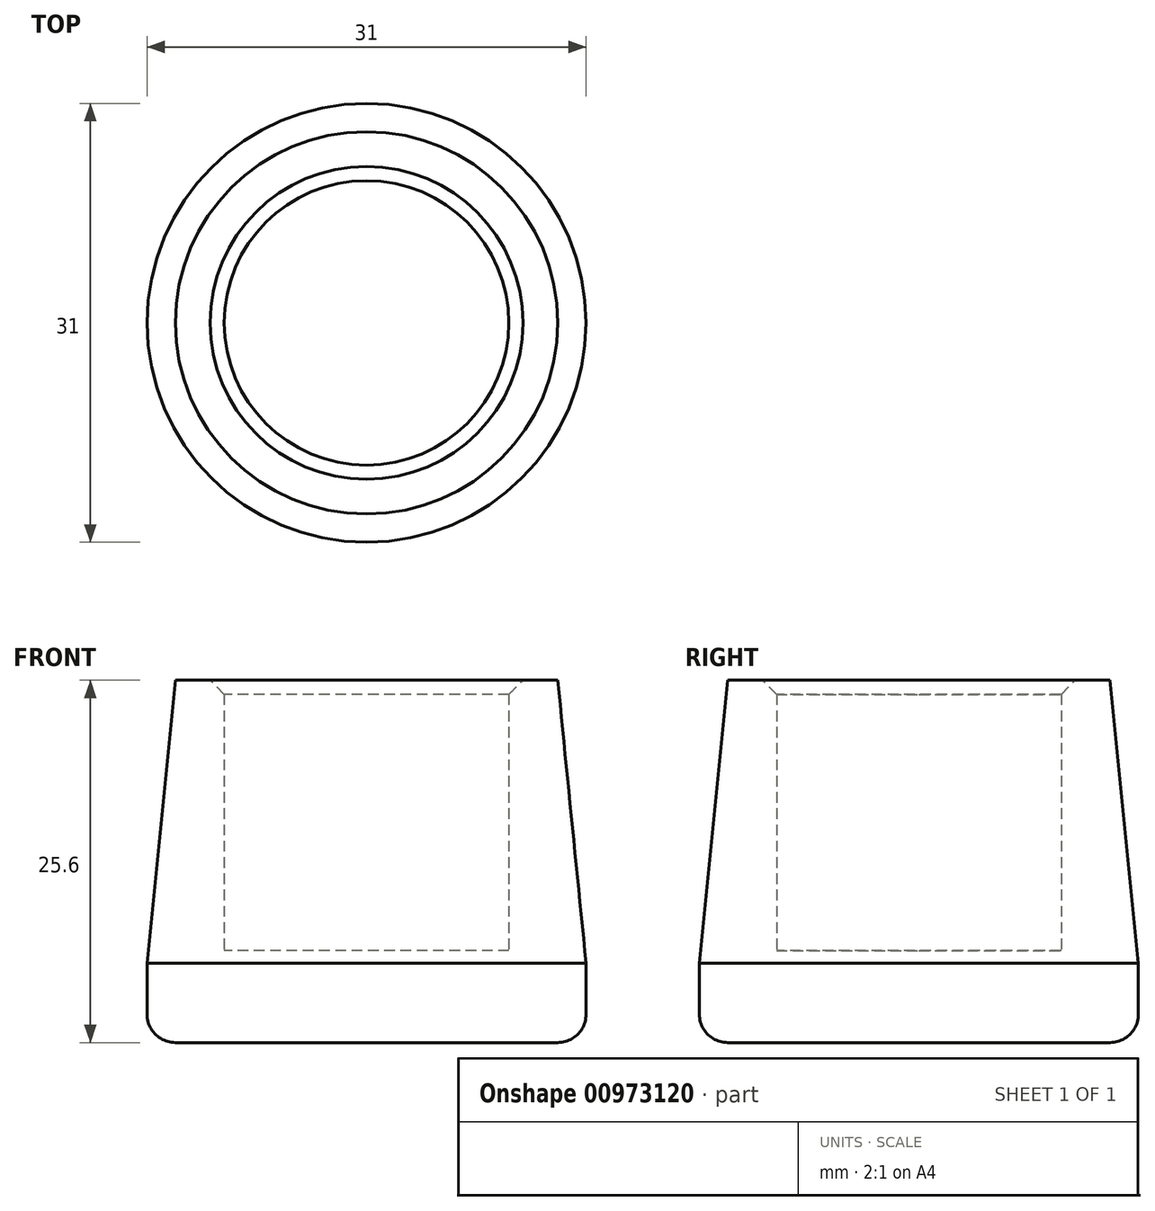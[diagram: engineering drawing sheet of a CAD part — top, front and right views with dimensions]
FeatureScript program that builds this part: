
annotation { "Feature Type Name" : "Feature", "Feature Type Description" : "" }
export const myFeature = defineFeature(function(context is Context, id is Id, definition is map)
    precondition{}
    {
        {
            var Q0;
            Q0=qCreatedBy(makeId("Top.planeOp"),FACE);
            var sketch = newSketch(context, id + "F0", { "sketchPlane" : qUnion([Q0])});
            skCircle(sketch, "E0", {"center": v(0, 0) * mm, "radius": 10.05 * mm});
            skCircle(sketch, "E1", {"center": v(0, 0) * mm, "radius": 15.5 * mm});
            skSolve(sketch);
        }
        {
            var Q0;
            Q0=makeQuery(id+"F0.imprint","IMPRINT",FACE,{"disambiguationData":[TD([[makeQuery(id+"F0.imprint","IMPRINT",EDGE,{"derivedFrom":sQuery(id+"F0.wireOp",EDGE,"E0")}),-1.0]])]});
            var Q1;
            Q1=makeQuery(id+"F0.imprint","IMPRINT",FACE,{"disambiguationData":[TD([[makeQuery(id+"F0.imprint","IMPRINT",EDGE,{"derivedFrom":sQuery(id+"F0.wireOp",EDGE,"E0")}),1.0]])]});
            extrude(context, id + "F1", {"entities" : qUnion([Q0, Q1]), "depth" : 6.5 * mm, "offsetDistance" : 25 * mm});
        }
        {
            var Q0;
            Q0=makeQuery(id+"F0.imprint","IMPRINT",FACE,{"disambiguationData":[TD([[makeQuery(id+"F0.imprint","IMPRINT",EDGE,{"derivedFrom":sQuery(id+"F0.wireOp",EDGE,"E0")}),-1.0]])]});
            extrude(context, id + "F2", {"entities" : qUnion([Q0]), "operationType" : NewBodyOperationType.ADD, "depth" : 25.6 * mm, "offsetDistance" : 25 * mm});
        }
        {
            var Q0;
            Q0=makeQuery(id+"F1.opExtrude","CAP_EDGE",EDGE,{"disambiguationData":[OSD([sQuery(id+"F0.wireOp",EDGE,"E1")])],"isStart":true});
            fillet(context, id + "F3", {"entities" : qUnion([Q0]), "radius" : 2 * mm, "tangentPropagation" : true, "allowEdgeOverflow" : false});
        }
        {
            var Q0;
            {var subQ0=sQuery(id+"F0.wireOp",EDGE,"E1");Q0=makeQuery(id+"F2.boolean.opBoolean","MERGE",FACE,{"derivedFrom":[makeQuery(id+"F1.opExtrude","SWEPT_FACE",FACE,{"disambiguationData":[OSD([subQ0])]}),makeQuery(id+"F2.opExtrude","SWEPT_FACE",FACE,{"disambiguationData":[OSD([subQ0])]})]});}
            chamfer(context, id + "F4", {"entities" : qUnion([Q0]), "chamferType" : ChamferType.TWO_OFFSETS, "width1" : 2 * mm, "oppositeDirection" : false, "width2" : 20 * mm, "tangentPropagation" : true});
        }
        {
            var Q0;
            Q0=makeQuery(id+"F2.opExtrude","CAP_EDGE",EDGE,{"disambiguationData":[OSD([sQuery(id+"F0.wireOp",EDGE,"E0")])],"isStart":false});
            chamfer(context, id + "F5", {"entities" : qUnion([Q0]), "width" : 1 * mm, "tangentPropagation" : true});
        }
    });
